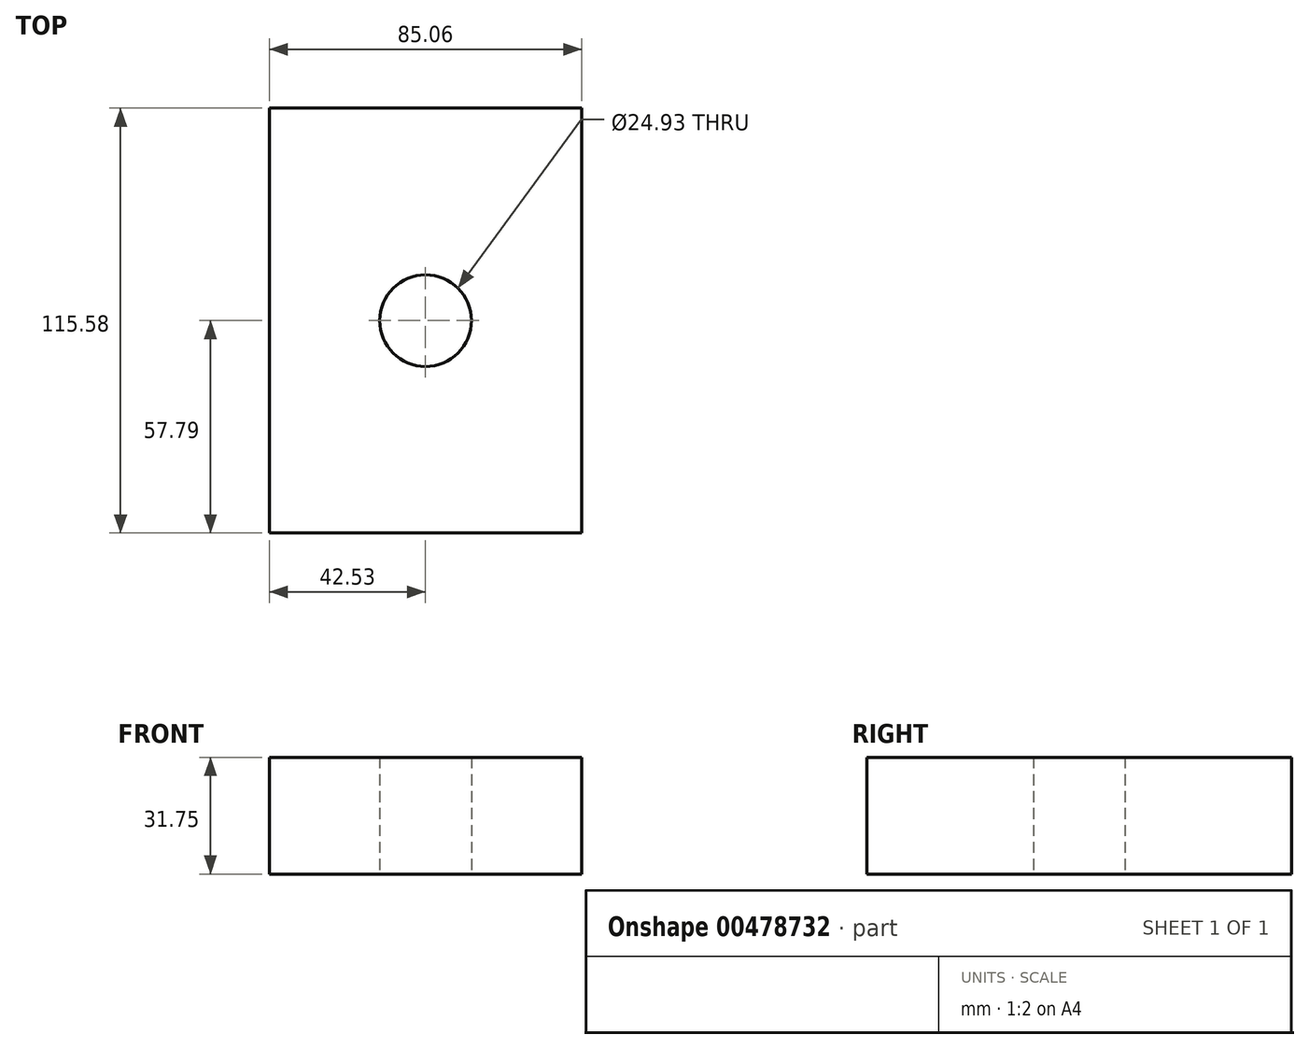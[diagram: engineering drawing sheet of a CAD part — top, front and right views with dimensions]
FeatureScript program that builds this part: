
annotation { "Feature Type Name" : "Feature", "Feature Type Description" : "" }
export const myFeature = defineFeature(function(context is Context, id is Id, definition is map)
    precondition{}
    {
        {
            var Q0;
            Q0=qCreatedBy(makeId("Top.planeOp"),FACE);
            var sketch = newSketch(context, id + "F0", { "sketchPlane" : qUnion([Q0])});
            skLineSegment(sketch, "E0.bottom", {"start": v(42.53, -57.79) * mm, "end": v(-42.53, -57.79) * mm});
            skLineSegment(sketch, "E0.top", {"start": v(42.53, 57.79) * mm, "end": v(-42.53, 57.79) * mm});
            skLineSegment(sketch, "E0.left", {"start": v(42.53, -57.79) * mm, "end": v(42.53, 57.79) * mm});
            skLineSegment(sketch, "E0.right", {"start": v(-42.53, -57.79) * mm, "end": v(-42.53, 57.79) * mm});
            skPoint(sketch, "E0.middle", {"position": v(0, 0) * mm});
            skSolve(sketch);
        }
        {
            var Q0;
            Q0 = qSketchRegion(id + "F0", true);
            extrude(context, id + "F1", {"entities" : qUnion([Q0]), "depth" : 6.35 * mm});
        }
        {
            var Q0;
            Q0=qCreatedBy(makeId("Top.planeOp"),FACE);
            var sketch = newSketch(context, id + "F2", { "sketchPlane" : qUnion([Q0])});
            skCircle(sketch, "E1", {"center": v(0, 0) * mm, "radius": 12.46 * mm});
            skSolve(sketch);
        }
        {
            var Q0;
            Q0 = qSketchRegion(id + "F2", true);
            extrude(context, id + "F3", {"entities" : qUnion([Q0]), "operationType" : NewBodyOperationType.REMOVE, "endBound" : BoundingType.THROUGH_ALL, "depth" : 25.4 * mm});
        }
        {
            var Q0;
            Q0=makeQuery(id+"F1.opExtrude","CAP_FACE",FACE,{"disambiguationData":[OSD([sQuery(id+"F0.wireOp",EDGE,"E0.bottom"),sQuery(id+"F0.wireOp",EDGE,"E0.top"),sQuery(id+"F0.wireOp",EDGE,"E0.left"),sQuery(id+"F0.wireOp",EDGE,"E0.right")])],"isStart":false});
            var sketch = newSketch(context, id + "F4", { "sketchPlane" : qUnion([Q0])});
            skCircle(sketch, "E2", {"center": v(30.23, 0) * mm, "radius": 12 * mm});
            skPoint(sketch, "E2.centerSnap0", {"position": v(42.53, 0) * mm});
            skSolve(sketch);
        }
        {
            var Q0;
            Q0=makeQuery(id+"F1.opExtrude","CAP_FACE",FACE,{"disambiguationData":[OSD([sQuery(id+"F0.wireOp",EDGE,"E0.bottom"),sQuery(id+"F0.wireOp",EDGE,"E0.top"),sQuery(id+"F0.wireOp",EDGE,"E0.left"),sQuery(id+"F0.wireOp",EDGE,"E0.right")])],"isStart":true});
            var Q1;
            Q1=makeQuery(id+"F4.imprint","IMPRINT",FACE,{"disambiguationData":[TD([[makeQuery(id+"F4.imprint","IMPRINT",EDGE,{"derivedFrom":sQuery(id+"F4.wireOp",EDGE,"E2")}),-1.0]])]});
            extrude(context, id + "F5", {"entities" : qUnion([Q0, Q1]), "operationType" : NewBodyOperationType.ADD, "depth" : 25.4 * mm});
        }
    });
